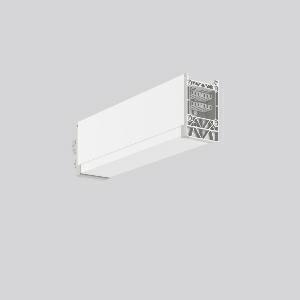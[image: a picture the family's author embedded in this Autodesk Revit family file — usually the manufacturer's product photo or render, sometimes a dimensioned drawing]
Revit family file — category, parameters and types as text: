
# Revit family: linedo_anfangseinspeisung_14pol_b_982678_012_493b
name_source: partatom
category: Lighting Fixtures
units: mm (PartAtom-declared; Revit-internal decimal feet)

## family parameters
Cut with Voids When Loaded = No
Host = Face
Light Source = No
Part Type = Normal
Room Calculation Point = No
Round Connector Dimension = Use Diameter
Shared = No

## types (1)
- LINEDO_Anfangseinspeisung_14pol_B
    Apparent Load = 0 VA
    Default Elevation = 1800 mm
    Description = Series: LINEDO
Initial power feed, 14-pole, connection socket. Housing: extruded aluminium profile, powder-coated. Cover made of plastic, surface like housing. LINEDO plug system, plastic, light grey. 2 cable glands (M20 and M25). Cable glands on side or on top. Easy connection for rigid or flexible wires.
Colour: white
Length: 312 mm
Width: 58 mm
Height: 91 mm
Weight: 680 g
    Height = 91 mm
    Lamp = 0 x
    Length = 312 mm
    Luminous efficacy = 0 lm/W
    Manufacturer = RZB
    ModVariant = No
    Model = 982678.012
    Mounting Place = Ceiling
    Mounting Type = Surface mounted
    Number of Poles = 1
    OnlyDefault = Yes
    Power Factor = 1
    Product Name = LINEDO_Anfangseinspeisung_14pol_B
    Product group = Surface mounted continuous line luminaire system
    ProductGroupID = 310
    Protection Class = Protection class I
    Protection Degree = Degree of protection
    RLX_Detail_Level = 1
    RLX_Emergency_Light_Flux = 0 lm
    RLX_Emergency_Type = 0
    RLX_Emergency_Type_DB = No
    RlxData = <blob elided: 13213 chars, md5=fa7a5cbe>
    Standby Power = 0 W
    System Light Flux = 0 lm
    System Power = 0 W
    Type Comments = Product without accessories
    Type Image = 982678.012.jpg
    URL = http://relux.com
    VarID = ---
    Voltage = 0 V
    Weight = 0.00 kg
    Width = 58 mm

## geometry (parser evidence)
native form markers: Sweep x9
no freeform markers — native parametric forms only
